# Revit family: Furniture_Chairs-Stools-Benches_Svedholm_Cylinder-bar-stool ORG
name_source: partatom
category: Furniture
revit_build: Autodesk Revit 2018 (Build: 20170223_1515(x64)
units: mm (PartAtom-declared; Revit-internal decimal feet)

## family parameters
Always vertical = No
Cut with Voids When Loaded = No
OmniClass Number = 23.21.23.13.17
OmniClass Title = Residential Stools
Room Calculation Point = No
Shared = No
Work Plane-Based = Yes

## types (1)
- ART - (306.600.005)
    BIMobject category = Chairs, Stools & Benches
    BIMobject category code = chairs-stools-benches
    BIMobject main category = Furniture
    BIMobject main category code = furniture
    Brand url = https://www.svedholm.se
    Default Elevation = 1219.2 mm  [stored 4 ft]
    Description = A bar stool with seat in tanned leather. Base of chrome-plated alternatively powder coated steel tube.
    Design country = Sweden
    Edition number = 1
    Manufacturer = Svedholm
    Manufacturer country = Sweden
    Manufacturer name = Svedholm
    Material main = Leather
    Material secondary = Polished Chrome
    Model = Cylinder bar stool
    Product Guid = 1441b8b9-134c-4ccd-979c-0762865f1ef3
    Product SKU = Cylinder-bar-stool
    Product data url = https://bimobject.com
    Product family = Cylinder
    Product group = Stools
    Product name = Cylinder bar stool
    Product url = https://www.svedholm.se
    QR code = http://bimobject.com
    Seat material = Svedholm - Textile - Tanned leather
    URL = https://www.svedholm.se

note: [stored X ft] marks values corroborated as IEEE doubles in the binary element streams (Revit-internal decimal feet)

## geometry (parser evidence)
native form markers: Sweep x3
no freeform markers — native parametric forms only
